# Revit family: 1426xxx Myos Spike Spot
name_source: partatom
category: Lighting Fixtures
units: mm (PartAtom-declared; Revit-internal decimal feet)

## family parameters
Always vertical = Yes
Cut with Voids When Loaded = No
Light Source = Yes
OmniClass Number = 23.80.70.00
OmniClass Title = Lighting
Part Type = Normal
Room Calculation Point = No
Round Connector Dimension = Use Diameter
Shared = No
Work Plane-Based = No

## types (2) — shared parameters
Color Filter = 16777215
Dimming Lamp Color Temperature Shift = <None>
Manufacturer URL - Europe and Rest of World = www.astrolighting.com
Manufacturer URL - North America = us.astrolighting.com
zero-valued in all types: Default Elevation

## per-type parameters (varying)
| type | Dimmable | Dimming Method | Driver Included | Driver Required | Efficacy (lm/W) | Electrical Class | Lamp | Length of Cable Supplied | Light Source Fixed | Location / IP Rating | Main Finish | Main Material | Photometric Web File | Power (W) | Product CCT | Product CRI | Product Dimensions (MM) | Product Location | Product Name | Product SKU | Product Weight (KG) | Tilt Angle |
| CE |  |  |  |  |  |  |  |  |  |  |  |  | generic |  | 2700K / 3000K | 80/ 90 |  |  |  | 1234567 |  | 60.00° |
| ETL | Yes | Control Gear Dependent | No | Constant Current 700mA | 27 | CE (Class III) | LED | 2700 (mm) | Yes | IP65 | Textured Black | Metal - Aluminium | 1426001_Myos_Photometry_IES_Iss.01.ies | 11.4 | 3000 | 90 | H150 L110 Ø40mm | Outdoor | Myos | 1426002 | 0.8 | 180.00° |

## geometry (parser evidence)
native form markers: Sweep x3
no freeform markers — native parametric forms only
